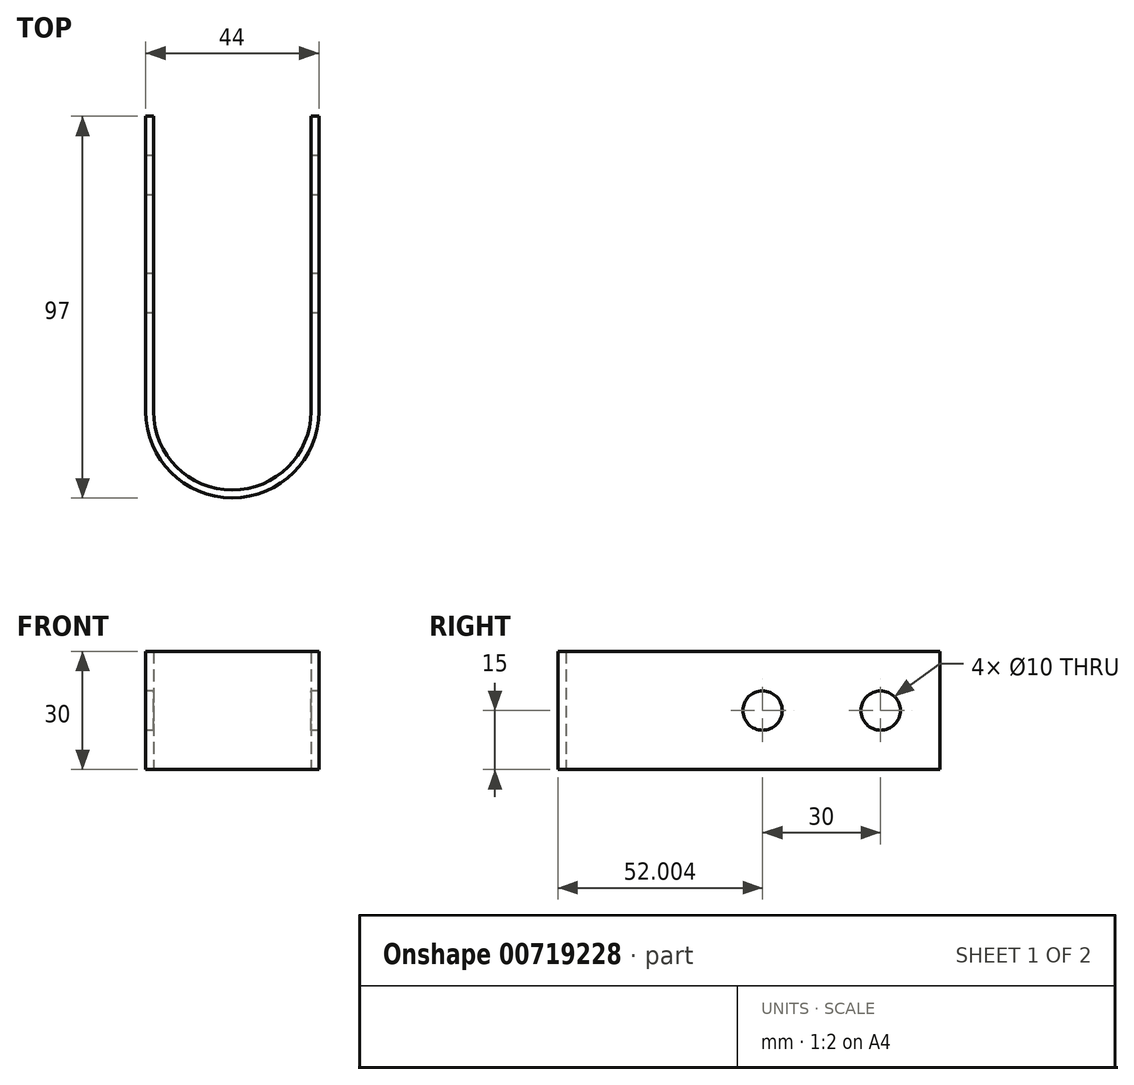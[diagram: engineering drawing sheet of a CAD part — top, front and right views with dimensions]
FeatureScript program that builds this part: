
annotation { "Feature Type Name" : "Feature", "Feature Type Description" : "" }
export const myFeature = defineFeature(function(context is Context, id is Id, definition is map)
    precondition{}
    {
        {
            var Q0;
            Q0=qCreatedBy(makeId("Top.planeOp"),FACE);
            var sketch = newSketch(context, id + "F0", { "sketchPlane" : qUnion([Q0])});
            skLineSegment(sketch, "E0", {"start": v(-27.4, 47.1) * mm, "end": v(-27.4, -27.9) * mm});
            skArc(sketch, "E1", {"start": v(-27.4, -27.9) * mm, "mid": v(-7.4, -47.9) * mm, "end": v(12.6, -27.9) * mm});
            skLineSegment(sketch, "E2", {"start": v(-7.4, -27.9) * mm, "end": v(-27.4, -27.9) * mm});
            skLineSegment(sketch, "E3", {"start": v(12.6, -27.9) * mm, "end": v(12.6, 47.1) * mm});
            skLineSegment(sketch, "E4.0", {"start": v(14.6, -27.9) * mm, "end": v(14.6, 47.1) * mm});
            skArc(sketch, "E4.1", {"start": v(-29.4, -27.9) * mm, "mid": v(-7.4, -49.9) * mm, "end": v(14.6, -27.9) * mm});
            skLineSegment(sketch, "E4.2", {"start": v(-29.4, 47.1) * mm, "end": v(-29.4, -27.9) * mm});
            skLineSegment(sketch, "E5", {"start": v(-29.4, 47.1) * mm, "end": v(-27.4, 47.1) * mm});
            skLineSegment(sketch, "E6", {"start": v(12.6, 47.1) * mm, "end": v(14.6, 47.1) * mm});
            skSolve(sketch);
        }
        {
            var Q0;
            Q0 = qSketchRegion(id + "F0", true);
            extrude(context, id + "F1", {"entities" : qUnion([Q0]), "depth" : 30 * mm, "offsetDistance" : 25 * mm});
        }
        {
            var Q0;
            Q0=makeQuery(id+"F1.opExtrude","SWEPT_FACE",FACE,{"disambiguationData":[OSD([sQuery(id+"F0.wireOp",EDGE,"E4.2")])]});
            var sketch = newSketch(context, id + "F2", { "sketchPlane" : qUnion([Q0])});
            skCircle(sketch, "E7", {"center": v(-32.1, 15) * mm, "radius": 5 * mm});
            skCircle(sketch, "E8", {"center": v(-2.1, 15) * mm, "radius": 5 * mm});
            skSolve(sketch);
        }
        {
            var Q0;
            Q0=makeQuery(id+"F2.imprint","IMPRINT",FACE,{"disambiguationData":[TD([[makeQuery(id+"F2.imprint","IMPRINT",EDGE,{"derivedFrom":sQuery(id+"F2.wireOp",EDGE,"E7")}),1.0]])]});
            var Q1;
            Q1=makeQuery(id+"F2.imprint","IMPRINT",FACE,{"disambiguationData":[TD([[makeQuery(id+"F2.imprint","IMPRINT",EDGE,{"derivedFrom":sQuery(id+"F2.wireOp",EDGE,"E8")}),1.0]])]});
            var Q2;
            Q2=makeQuery(id+"F1.opExtrude","SWEPT_FACE",FACE,{"disambiguationData":[OSD([sQuery(id+"F0.wireOp",EDGE,"E4.0")])]});
            extrude(context, id + "F3", {"entities" : qUnion([Q0, Q1]), "operationType" : NewBodyOperationType.REMOVE, "endBound" : BoundingType.UP_TO_SURFACE, "oppositeDirection" : true, "depth" : 25 * mm, "endBoundEntityFace" : qUnion([Q2]), "offsetDistance" : 25 * mm});
        }
    });
